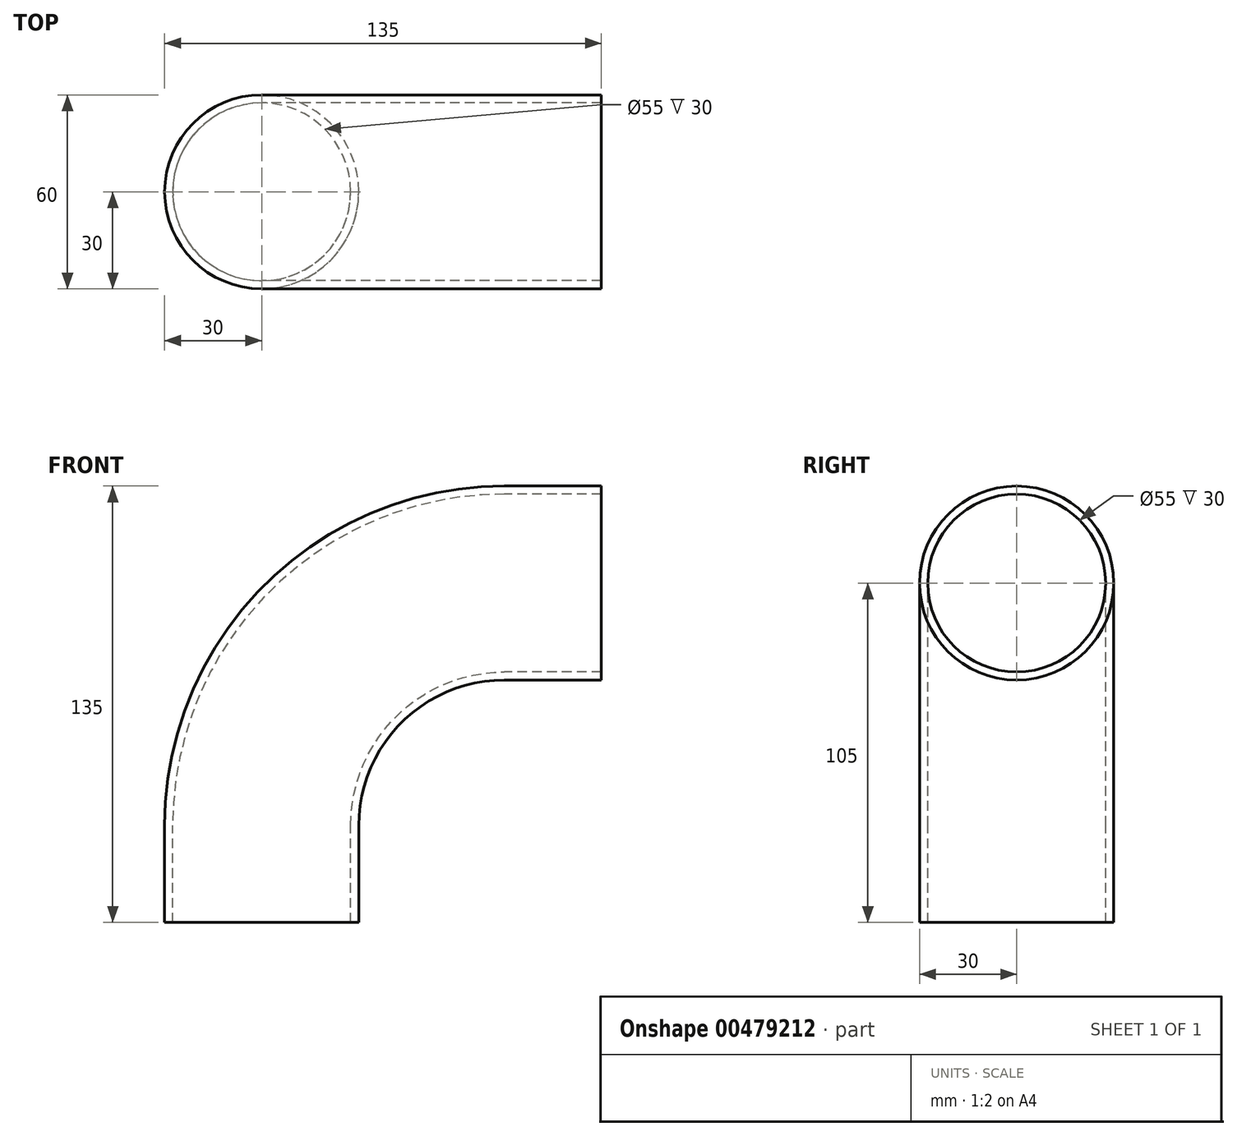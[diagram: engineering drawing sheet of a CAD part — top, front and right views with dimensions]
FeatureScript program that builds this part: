
annotation { "Feature Type Name" : "Feature", "Feature Type Description" : "" }
export const myFeature = defineFeature(function(context is Context, id is Id, definition is map)
    precondition{}
    {
        {
            var Q0;
            Q0=qCreatedBy(makeId("Top.planeOp"),FACE);
            var sketch = newSketch(context, id + "F0", { "sketchPlane" : qUnion([Q0])});
            skCircle(sketch, "E0", {"center": v(0, 0) * mm, "radius": 27.5 * mm});
            skCircle(sketch, "E1", {"center": v(0, 0) * mm, "radius": 30 * mm});
            skSolve(sketch);
        }
        {
            var Q0;
            Q0=qCreatedBy(makeId("Front.planeOp"),FACE);
            var sketch = newSketch(context, id + "F1", { "sketchPlane" : qUnion([Q0])});
            skArc(sketch, "E2", {"start": v(75, 75) * mm, "mid": v(21.97, 53.03) * mm, "end": v(0, 0) * mm});
            skLineSegment(sketch, "E3", {"start": v(0, 0) * mm, "end": v(75, 0) * mm});
            skLineSegment(sketch, "E4", {"start": v(75, 0) * mm, "end": v(75, 75) * mm});
            skSolve(sketch);
        }
        {
            var Q0;
            Q0=makeQuery(id+"F0.imprint","IMPRINT",FACE,{"disambiguationData":[TD([[makeQuery(id+"F0.imprint","IMPRINT",EDGE,{"derivedFrom":sQuery(id+"F0.wireOp",EDGE,"E0")}),-1.0]])]});
            var Q1;
            Q1=sQuery(id+"F1.wireOp",EDGE,"E2");
            sweep(context, id + "F2", {"profiles" : qUnion([Q0]), "path" : qUnion([Q1])});
        }
        {
            var Q0;
            Q0=makeQuery(id+"F2.opSweep","CAP_FACE",FACE,{"disambiguationData":[OSD([sQuery(id+"F0.wireOp",EDGE,"E0"),sQuery(id+"F0.wireOp",EDGE,"E1"),sQuery(id+"F1.wireOp",VERTEX,"E2.start")])],"isStart":false});
            var sketch = newSketch(context, id + "F3", { "sketchPlane" : qUnion([Q0])});
            skCircle(sketch, "E5", {"center": v(0, 75) * mm, "radius": 27.5 * mm});
            skCircle(sketch, "E6", {"center": v(0, 75) * mm, "radius": 30 * mm});
            skSolve(sketch);
        }
        {
            var Q0;
            Q0=makeQuery(id+"F3.imprint","IMPRINT",FACE,{"disambiguationData":[TD([[makeQuery(id+"F3.imprint","IMPRINT",EDGE,{"derivedFrom":sQuery(id+"F3.wireOp",EDGE,"E5")}),-1.0]])]});
            extrude(context, id + "F4", {"entities" : qUnion([Q0]), "operationType" : NewBodyOperationType.ADD, "depth" : 30 * mm});
        }
        {
            var Q0;
            Q0=makeQuery(id+"F2.opSweep","CAP_FACE",FACE,{"disambiguationData":[OSD([sQuery(id+"F0.wireOp",EDGE,"E0"),sQuery(id+"F0.wireOp",EDGE,"E1"),sQuery(id+"F1.wireOp",VERTEX,"E2.end")])],"isStart":true});
            extrude(context, id + "F5", {"entities" : qUnion([Q0]), "operationType" : NewBodyOperationType.ADD, "depth" : 30 * mm});
        }
    });
